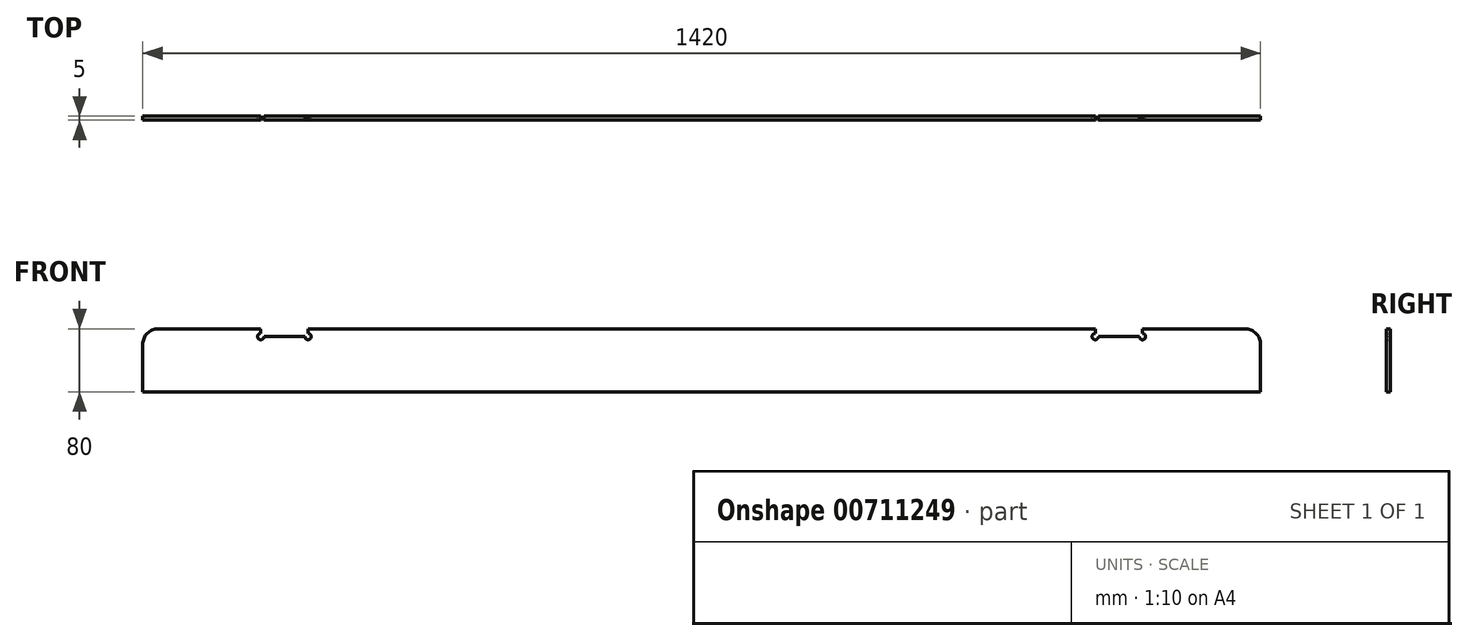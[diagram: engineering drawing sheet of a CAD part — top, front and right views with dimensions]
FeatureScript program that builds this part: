
annotation { "Feature Type Name" : "Feature", "Feature Type Description" : "" }
export const myFeature = defineFeature(function(context is Context, id is Id, definition is map)
    precondition{}
    {
        {
            var Q0;
            Q0=qCreatedBy(makeId("Front.planeOp"),FACE);
            var sketch = newSketch(context, id + "F0", { "sketchPlane" : qUnion([Q0])});
            skLineSegment(sketch, "E0.bottom", {"start": v(-690, 40) * mm, "end": v(-560, 40) * mm});
            skLineSegment(sketch, "E0.top", {"start": v(-710, -40) * mm, "end": v(710, -40) * mm});
            skLineSegment(sketch, "E0.left", {"start": v(-710, 20) * mm, "end": v(-710, -40) * mm});
            skLineSegment(sketch, "E0.right", {"start": v(710, 20) * mm, "end": v(710, -40) * mm});
            skPoint(sketch, "E0.middle", {"position": v(0, 0) * mm});
            skLineSegment(sketch, "E1.0", {"start": v(-560, 40) * mm, "end": v(-560, 34) * mm});
            skLineSegment(sketch, "E2.0", {"start": v(-500, 40) * mm, "end": v(-500, 34) * mm});
            skLineSegment(sketch, "E3.0", {"start": v(-556, 30) * mm, "end": v(-504, 30) * mm});
            skLineSegment(sketch, "E4.0", {"start": v(560, 40) * mm, "end": v(560, 34) * mm});
            skLineSegment(sketch, "E5.0", {"start": v(500, 40) * mm, "end": v(500, 34) * mm});
            skLineSegment(sketch, "E6.trimOffspring", {"start": v(504, 30) * mm, "end": v(556, 30) * mm});
            skLineSegment(sketch, "E7.trimOffspring", {"start": v(-500, 40) * mm, "end": v(500, 40) * mm});
            skLineSegment(sketch, "E8.trimOffspring", {"start": v(560, 40) * mm, "end": v(690, 40) * mm});
            skPoint(sketch, "E9.visualSharp", {"position": v(-710, 40) * mm});
            skArc(sketch, "E9.filletArc", {"start": v(-690, 40) * mm, "mid": v(-704.14, 34.14) * mm, "end": v(-710, 20) * mm});
            skArc(sketch, "E10", {"start": v(-560, 34) * mm, "mid": v(-562.83, 27.17) * mm, "end": v(-556, 30) * mm});
            skArc(sketch, "E11", {"start": v(-504, 30) * mm, "mid": v(-497.17, 27.17) * mm, "end": v(-500, 34) * mm});
            skArc(sketch, "E12", {"start": v(556, 30) * mm, "mid": v(562.83, 27.17) * mm, "end": v(560, 34) * mm});
            skArc(sketch, "E13", {"start": v(500, 34) * mm, "mid": v(497.17, 27.17) * mm, "end": v(504, 30) * mm});
            skPoint(sketch, "E14.visualSharp", {"position": v(710, 40) * mm});
            skArc(sketch, "E14.filletArc", {"start": v(710, 20) * mm, "mid": v(704.14, 34.14) * mm, "end": v(690, 40) * mm});
            skSolve(sketch);
        }
        {
            var Q0;
            Q0=makeQuery(id+"F0.imprint","IMPRINT",FACE,{"disambiguationData":[TD([[makeQuery(id+"F0.imprint","IMPRINT",EDGE,{"derivedFrom":sQuery(id+"F0.wireOp",EDGE,"E0.bottom")}),-1.0]])]});
            extrude(context, id + "F1", {"entities" : qUnion([Q0]), "depth" : 5 * mm, "offsetDistance" : 25 * mm});
        }
    });
